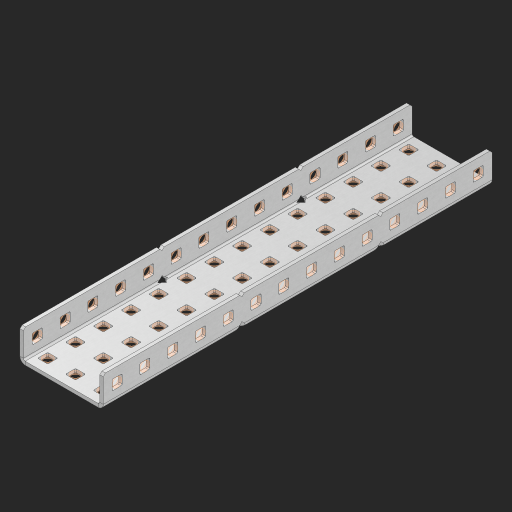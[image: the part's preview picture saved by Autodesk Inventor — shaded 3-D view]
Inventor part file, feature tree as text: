
AUTODESK INVENTOR PART (.ipt)
format: ipt  version: 2023 (Build 270158000, 158)  size: 1,084,416 bytes
history: native  units: in
note: dims shown in document units (in); Inventor stores cm internally (conversion verified against a paired STEP export)
features: other x75, extrude x69, sheet_metal_op x10, sketch x8, mirror x1, pattern_linear x1, chamfer x1
ambient origin geometry x8: Origin, YZ Plane, XZ Plane, XY Plane, X Axis, Y Axis, Z Axis, Center Point
bodies: Solid1 (feature_tree), Body (feature_tree)
feature tree (165):
  other  "Flange Pattern Plane"
  sheet_metal_op  "Flange Pattern"
  sheet_metal_op  "Body Pattern"
  other  "Arc Length"
  mirror  "Notch Mirror"
  pattern_linear  "Notch Pattern"  Spacing1=0.25in  [1 undecoded]
  chamfer  "End Chamfer"
  extrude  "Half Cut"  Depth=0.0625in
  sketch  "Sketch1"  dims[d0=1.5in]
  other  "Plate1"
  sketch  "Sketch2"  dims[d1=7.0in]
  other  "Plate2"
  sheet_metal_op  "Bend1"
  sheet_metal_op  "Corner1"
  sketch  "Sketch3"  dims[d2=0.0625in]
  other  "Flange Pattern Sketch"
  sketch  "Sketch7"  dims[d3=0.0625in]
  other  "Srf1"
  other  "Srf2"
  sketch  "Sketch8"  dims[d4=0.0312in]
  sketch  "Sketch9"  dims[d5=0.125in]
  other  "Srf91"
  sheet_metal_op  "Body Pattern Sketch"
  other  "Srf92"
  sketch  "Sketch13"  dims[d6=0.0625in]
  sketch  "Sketch14"  dims[d7=0.5in d8=90.0deg d9=0.0312in d10=0.25in d11=0.0625in d12=0.0625in d16=0.182in d17=0.02in d18=0.0625in d19=0.0in d20=0.25in d21=0.25in d46=0.172in d47=1.0in d48=0.0in d49=0.182in d50=0.02in d51=0.25in d52=0.25in d53=0.0625in d54=0.0in d55=0.172in d56=1.0in d57=0.0in d60=5.5118in d62=0.5in d63=1.1811in d65=0.5in d85=0.1473in d86=0.1782in d88=0.04in d89=0.0625in d90=0.0in d91=0.04in d92=0.0491in d95=2.5in d96=0.04in d97=0.25in d98=45.0deg d101=0.0in d102=2.497in d131=1.5in d132=5.5118in d134=0.5in d139=0.5in]
  other  "Srf856"
  other  "Srf1310"
  other  "Srf1311"
  other  "Srf1312"
  other  "Srf1376"
  other  "Srf1377"
  other  "Srf1728"
  other  "Srf1755"
  other  "Srf1878"
  other  "Srf1879"
  other  "Srf1880"
  other  "Srf1881"
  other  "Srf1882"
  other  "Srf1883"
  other  "Srf1884"
  other  "Srf1885"
  other  "Srf1886"
  other  "Srf1887"
  other  "Srf1888"
  other  "Srf1889"
  other  "Srf1890"
  other  "Srf1891"
  other  "Srf1892"
  other  "Srf1893"
  other  "Srf1894"
  other  "Srf1895"
  other  "Srf1896"
  other  "Srf1897"
  other  "Srf1898"
  other  "Srf1899"
  other  "Srf1942"
  other  "Srf1943"
  other  "Srf1944"
  other  "Srf1945"
  other  "Srf1946"
  other  "Srf1947"
  other  "Srf1948"
  other  "Srf1949"
  other  "Srf1950"
  other  "Srf1951"
  other  "Srf1952"
  other  "Srf1953"
  other  "Srf1954"
  other  "Srf1955"
  other  "Srf1956"
  other  "Srf1957"
  other  "Srf1958"
  other  "Srf1959"
  other  "Srf1960"
  other  "Srf1961"
  other  "Srf1962"
  other  "Srf1963"
  other  "Srf1964"
  other  "Srf1965"
  other  "Srf1966"
  other  "Srf1967"
  other  "Srf1968"
  other  "Srf1969"
  other  "Srf1970"
  other  "Srf1971"
  other  "Srf1972"
  other  "Srf1973"
  other  "Srf1974"
  other  "Srf1975"
  other  "Srf1976"
  other  "Srf1977"
  sheet_metal_op  "Flange Stamp"
  sheet_metal_op  "Flange Circle"
  sheet_metal_op  "Body Stamp"
  sheet_metal_op  "Body Circle"
  sheet_metal_op  "Notch"
  extrude  "ExtrusionSrf2"  Depth=0.0625in
  extrude  "ExtrusionSrf92"  Depth=1.5in
  extrude  "ExtrusionSrf856"  Depth=0.02in
  extrude  "ExtrusionSrf1310"  Depth=0.0625in
  extrude  "ExtrusionSrf1311"  TaperAngle=0.0deg  [1 undecoded]
  extrude  "ExtrusionSrf1312"  Depth=0.25in
  extrude  "ExtrusionSrf1376"  Depth=0.25in
  extrude  "ExtrusionSrf1377"  Depth=1.5in
  extrude  "ExtrusionSrf1728"  Depth=1.5in TaperAngle=0.0deg
  extrude  "ExtrusionSrf1755"  Depth=1.5in
  extrude  "ExtrusionSrf1878"  Depth=0.02in
  extrude  "ExtrusionSrf1879"  Depth=0.25in
  extrude  "ExtrusionSrf1880"  Depth=0.25in
  extrude  "ExtrusionSrf1881"  Depth=0.0625in
  extrude  "ExtrusionSrf1882"  TaperAngle=0.0deg  [1 undecoded]
  extrude  "ExtrusionSrf1883"  Depth=1.5in
  extrude  "ExtrusionSrf1884"  Depth=1.5in TaperAngle=0.0deg
  extrude  "ExtrusionSrf1885"  Depth=1.5in
  extrude  "ExtrusionSrf1886"  Depth=1.5in
  extrude  "ExtrusionSrf1887"  Depth=1.5in
  extrude  "ExtrusionSrf1888"  Depth=1.5in
  extrude  "ExtrusionSrf1889"  Depth=1.5in
  extrude  "ExtrusionSrf1890"  Depth=0.0625in
  extrude  "ExtrusionSrf1891"  TaperAngle=0.0deg  [1 undecoded]
  extrude  "ExtrusionSrf1892"  Depth=1.5in
  extrude  "ExtrusionSrf1893"  Depth=1.5in
  extrude  "ExtrusionSrf1894"  Depth=1.5in
  extrude  "ExtrusionSrf1895"  Depth=0.25in TaperAngle=45.0deg
  extrude  "ExtrusionSrf1896"  TaperAngle=0.0deg  [1 undecoded]
  extrude  "ExtrusionSrf1897"  Depth=1.5in
  extrude  "ExtrusionSrf1898"  Depth=1.5in
  extrude  "ExtrusionSrf1899"  Depth=1.5in
  extrude  "ExtrusionSrf1942"  Depth=1.5in
  extrude  "ExtrusionSrf1943"  Depth=1.5in
  extrude  "ExtrusionSrf1944"  [1 undecoded]
  extrude  "ExtrusionSrf1945"  [1 undecoded]
  extrude  "ExtrusionSrf1946"  [1 undecoded]
  extrude  "ExtrusionSrf1947"  [1 undecoded]
  extrude  "ExtrusionSrf1948"  [1 undecoded]
  extrude  "ExtrusionSrf1949"  [1 undecoded]
  extrude  "ExtrusionSrf1950"  [1 undecoded]
  extrude  "ExtrusionSrf1951"  [1 undecoded]
  extrude  "ExtrusionSrf1952"  [1 undecoded]
  extrude  "ExtrusionSrf1953"  [1 undecoded]
  extrude  "ExtrusionSrf1954"  [1 undecoded]
  extrude  "ExtrusionSrf1955"  [1 undecoded]
  extrude  "ExtrusionSrf1956"  [1 undecoded]
  extrude  "ExtrusionSrf1957"  [1 undecoded]
  extrude  "ExtrusionSrf1958"  [1 undecoded]
  extrude  "ExtrusionSrf1959"  [1 undecoded]
  extrude  "ExtrusionSrf1960"  [1 undecoded]
  extrude  "ExtrusionSrf1961"  [1 undecoded]
  extrude  "ExtrusionSrf1962"  [1 undecoded]
  extrude  "ExtrusionSrf1963"  [1 undecoded]
  extrude  "ExtrusionSrf1964"  [1 undecoded]
  extrude  "ExtrusionSrf1965"  [1 undecoded]
  extrude  "ExtrusionSrf1966"  [1 undecoded]
  extrude  "ExtrusionSrf1967"  [1 undecoded]
  extrude  "ExtrusionSrf1968"  [1 undecoded]
  extrude  "ExtrusionSrf1969"  [1 undecoded]
  extrude  "ExtrusionSrf1970"  [1 undecoded]
  extrude  "ExtrusionSrf1971"  [1 undecoded]
  extrude  "ExtrusionSrf1972"  [1 undecoded]
  extrude  "ExtrusionSrf1973"  [1 undecoded]
  extrude  "ExtrusionSrf1974"  [1 undecoded]
  extrude  "ExtrusionSrf1975"  [1 undecoded]
  extrude  "ExtrusionSrf1976"  [1 undecoded]
  extrude  "ExtrusionSrf1977"  [1 undecoded]
note: 39 required parameter values undecoded (feature->parameter linkage not recoverable at this tier; creation-order binding heuristic only, values carry confidence <= 0.55)
